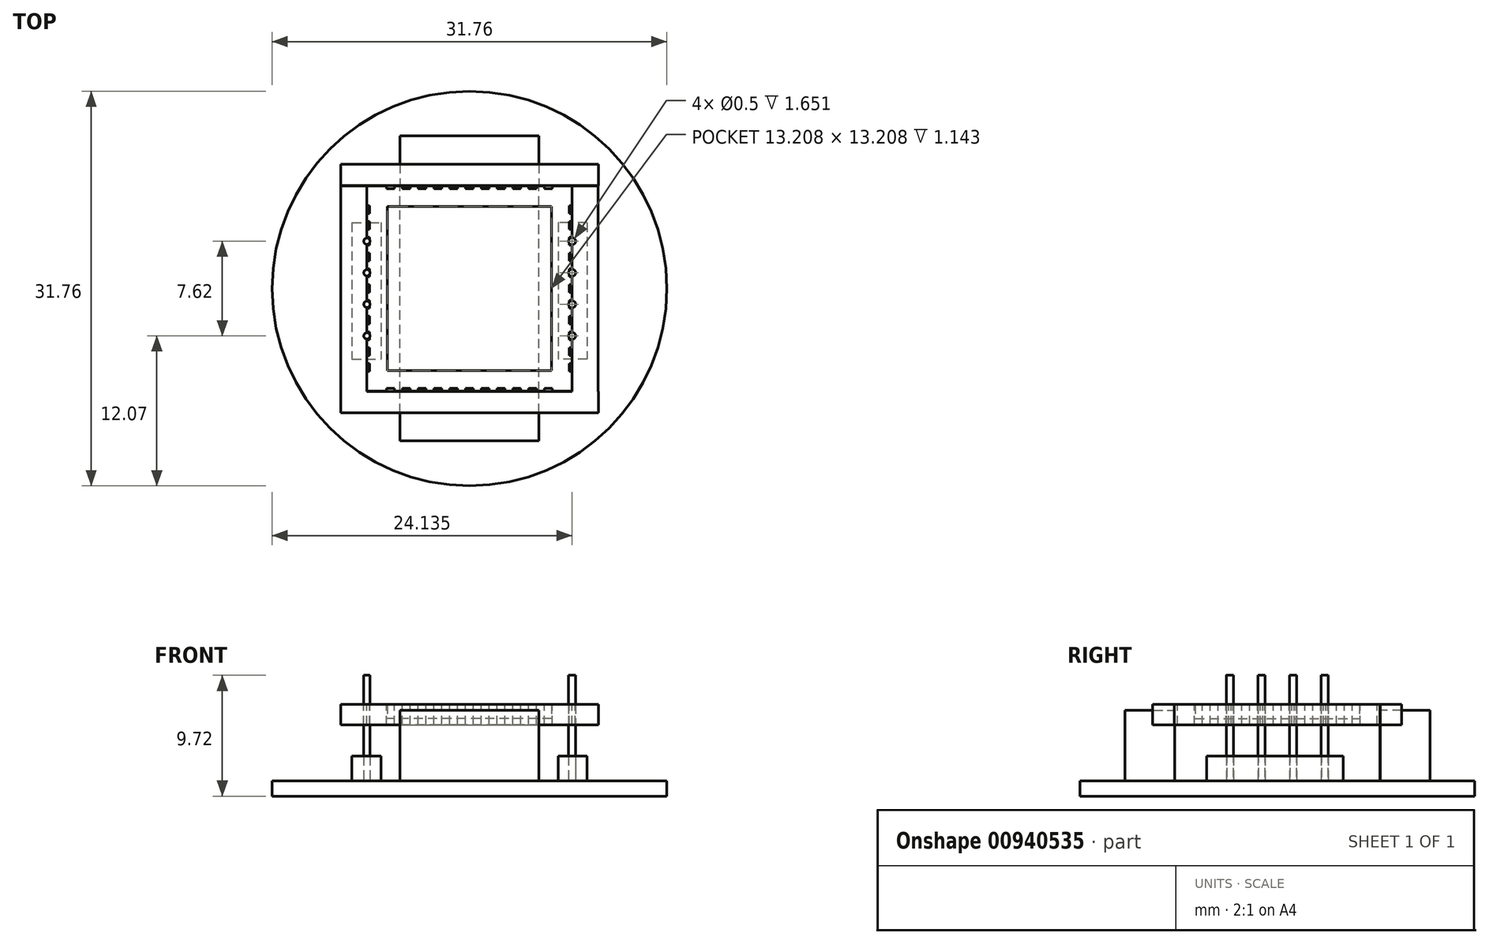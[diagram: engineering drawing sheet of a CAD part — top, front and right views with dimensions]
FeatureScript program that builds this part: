
annotation { "Feature Type Name" : "Feature", "Feature Type Description" : "" }
export const myFeature = defineFeature(function(context is Context, id is Id, definition is map)
    precondition{}
    {
        {
            var Q0;
            Q0=qCreatedBy(makeId("Top.planeOp"),FACE);
            var sketch = newSketch(context, id + "F0", { "sketchPlane" : qUnion([Q0])});
            skLineSegment(sketch, "E0.bottom", {"start": v(8.26, -8.26) * mm, "end": v(-8.26, -8.26) * mm});
            skLineSegment(sketch, "E0.top", {"start": v(8.26, 8.26) * mm, "end": v(-8.26, 8.26) * mm});
            skLineSegment(sketch, "E0.left", {"start": v(8.26, -8.26) * mm, "end": v(8.26, 8.26) * mm});
            skLineSegment(sketch, "E0.right", {"start": v(-8.26, -8.26) * mm, "end": v(-8.26, 8.26) * mm});
            skPoint(sketch, "E0.middle", {"position": v(0, 0) * mm});
            skLineSegment(sketch, "E1.bottom", {"start": v(6.6, -6.6) * mm, "end": v(-6.6, -6.6) * mm});
            skLineSegment(sketch, "E1.top", {"start": v(6.6, 6.6) * mm, "end": v(-6.6, 6.6) * mm});
            skLineSegment(sketch, "E1.left", {"start": v(6.6, -6.6) * mm, "end": v(6.6, 6.6) * mm});
            skLineSegment(sketch, "E1.right", {"start": v(-6.6, -6.6) * mm, "end": v(-6.6, 6.6) * mm});
            skSolve(sketch);
        }
        {
            var Q0;
            Q0=makeQuery(id+"F0.imprint","IMPRINT",FACE,{"disambiguationData":[TD([[makeQuery(id+"F0.imprint","IMPRINT",EDGE,{"derivedFrom":sQuery(id+"F0.wireOp",EDGE,"E1.bottom")}),-1.0]])]});
            extrude(context, id + "F1", {"entities" : qUnion([Q0]), "depth" : 0.5 * mm, "offsetDistance" : 25 * mm});
        }
        {
            var Q0;
            Q0=makeQuery(id+"F0.imprint","IMPRINT",FACE,{"disambiguationData":[TD([[makeQuery(id+"F0.imprint","IMPRINT",EDGE,{"derivedFrom":sQuery(id+"F0.wireOp",EDGE,"E0.bottom")}),-1.0]])]});
            extrude(context, id + "F2", {"entities" : qUnion([Q0]), "operationType" : NewBodyOperationType.ADD, "depth" : 1.65 * mm, "offsetDistance" : 25 * mm});
        }
        {
            var Q0;
            Q0=makeQuery(id+"F2.opExtrude","SWEPT_FACE",FACE,{"disambiguationData":[OSD([sQuery(id+"F0.wireOp",EDGE,"E0.bottom")])]});
            var sketch = newSketch(context, id + "F3", { "sketchPlane" : qUnion([Q0])});
            skLineSegment(sketch, "E2.bottom", {"start": v(-6.03, 0) * mm, "end": v(-6.67, 0) * mm});
            skLineSegment(sketch, "E2.top", {"start": v(-6.03, 1.65) * mm, "end": v(-6.67, 1.65) * mm});
            skLineSegment(sketch, "E2.left", {"start": v(-6.03, 0) * mm, "end": v(-6.03, 1.65) * mm});
            skLineSegment(sketch, "E2.right", {"start": v(-6.67, 0) * mm, "end": v(-6.67, 1.65) * mm});
            skPoint(sketch, "E2.middle", {"position": v(-6.35, 0.83) * mm});
            skLineSegment(sketch, "E3.bottom", {"start": v(-4.76, 0) * mm, "end": v(-5.4, 0) * mm});
            skLineSegment(sketch, "E3.top", {"start": v(-4.76, 1.65) * mm, "end": v(-5.4, 1.65) * mm});
            skLineSegment(sketch, "E3.left", {"start": v(-4.76, 0) * mm, "end": v(-4.76, 1.65) * mm});
            skLineSegment(sketch, "E3.right", {"start": v(-5.4, 0) * mm, "end": v(-5.4, 1.65) * mm});
            skPoint(sketch, "E3.middle", {"position": v(-5.08, 0.83) * mm});
            skLineSegment(sketch, "E4.MirrorCS", {"start": v(-4.13, 0) * mm, "end": v(-3.5, 0) * mm});
            skLineSegment(sketch, "E5.MirrorCS", {"start": v(-4.13, 1.65) * mm, "end": v(-3.5, 1.65) * mm});
            skPoint(sketch, "E6.MirrorP", {"position": v(-2.8, 0.8) * mm});
            skLineSegment(sketch, "E7.MirrorCS", {"start": v(-4.13, 0) * mm, "end": v(-4.13, 1.65) * mm});
            skLineSegment(sketch, "E8.MirrorCS", {"start": v(-2.86, 0) * mm, "end": v(-2.22, 0) * mm});
            skLineSegment(sketch, "E9.MirrorCS", {"start": v(-2.22, 0) * mm, "end": v(-2.22, 1.65) * mm});
            skLineSegment(sketch, "E10.MirrorCS", {"start": v(-2.86, 0) * mm, "end": v(-2.86, 1.65) * mm});
            skPoint(sketch, "E11.MirrorP", {"position": v(-4.1, 0.84) * mm});
            skLineSegment(sketch, "E12.MirrorCS", {"start": v(-3.5, 0) * mm, "end": v(-3.5, 1.65) * mm});
            skLineSegment(sketch, "E13.MirrorCS", {"start": v(-2.86, 1.65) * mm, "end": v(-2.22, 1.65) * mm});
            skLineSegment(sketch, "E14.MirrorCS", {"start": v(0.32, 0) * mm, "end": v(-0.32, 0) * mm});
            skPoint(sketch, "E15.MirrorP", {"position": v(-0.3, 0.84) * mm});
            skLineSegment(sketch, "E16.MirrorCS", {"start": v(-1.59, 0) * mm, "end": v(-1.59, 1.65) * mm});
            skLineSegment(sketch, "E17.MirrorCS", {"start": v(0.95, 0) * mm, "end": v(0.95, 1.65) * mm});
            skLineSegment(sketch, "E18.MirrorCS", {"start": v(-0.32, 0) * mm, "end": v(-0.32, 1.65) * mm});
            skLineSegment(sketch, "E19.MirrorCS", {"start": v(0.32, 0) * mm, "end": v(0.32, 1.65) * mm});
            skPoint(sketch, "E20.MirrorP", {"position": v(-1.56, 0.82) * mm});
            skLineSegment(sketch, "E21.MirrorCS", {"start": v(2.22, 1.65) * mm, "end": v(2.86, 1.65) * mm});
            skLineSegment(sketch, "E22.MirrorCS", {"start": v(2.86, 0) * mm, "end": v(2.86, 1.65) * mm});
            skLineSegment(sketch, "E23.MirrorCS", {"start": v(-0.95, 1.65) * mm, "end": v(-1.59, 1.65) * mm});
            skPoint(sketch, "E24.MirrorP", {"position": v(2.22, 0.83) * mm});
            skLineSegment(sketch, "E25.MirrorCS", {"start": v(-0.95, 0) * mm, "end": v(-1.59, 0) * mm});
            skLineSegment(sketch, "E26.MirrorCS", {"start": v(-0.95, 0) * mm, "end": v(-0.95, 1.65) * mm});
            skLineSegment(sketch, "E27.MirrorCS", {"start": v(0.95, 0) * mm, "end": v(1.59, 0) * mm});
            skLineSegment(sketch, "E28.MirrorCS", {"start": v(0.32, 1.65) * mm, "end": v(-0.32, 1.65) * mm});
            skLineSegment(sketch, "E29.MirrorCS", {"start": v(1.59, 0) * mm, "end": v(1.59, 1.65) * mm});
            skLineSegment(sketch, "E30.MirrorCS", {"start": v(0.95, 1.65) * mm, "end": v(1.59, 1.65) * mm});
            skLineSegment(sketch, "E31.MirrorCS", {"start": v(2.22, 0) * mm, "end": v(2.22, 1.65) * mm});
            skLineSegment(sketch, "E32.MirrorCS", {"start": v(2.22, 0) * mm, "end": v(2.86, 0) * mm});
            skPoint(sketch, "E33.MirrorP", {"position": v(0.95, 0.83) * mm});
            skLineSegment(sketch, "E34.MirrorCS", {"start": v(3.5, 0) * mm, "end": v(3.5, 1.65) * mm});
            skPoint(sketch, "E35.MirrorP", {"position": v(5.96, 0.82) * mm});
            skLineSegment(sketch, "E36.MirrorCS", {"start": v(6.03, 0) * mm, "end": v(6.67, 0) * mm});
            skLineSegment(sketch, "E37.MirrorCS", {"start": v(6.03, 0) * mm, "end": v(6.03, 1.65) * mm});
            skLineSegment(sketch, "E38.MirrorCS", {"start": v(5.4, 1.65) * mm, "end": v(4.76, 1.65) * mm});
            skPoint(sketch, "E39.MirrorP", {"position": v(4.76, 0.83) * mm});
            skLineSegment(sketch, "E40.MirrorCS", {"start": v(6.67, 0) * mm, "end": v(6.67, 1.65) * mm});
            skLineSegment(sketch, "E41.MirrorCS", {"start": v(5.4, 0) * mm, "end": v(5.4, 1.65) * mm});
            skLineSegment(sketch, "E42.MirrorCS", {"start": v(4.13, 0) * mm, "end": v(4.13, 1.65) * mm});
            skLineSegment(sketch, "E43.MirrorCS", {"start": v(4.76, 0) * mm, "end": v(4.76, 1.65) * mm});
            skLineSegment(sketch, "E44.MirrorCS", {"start": v(4.13, 0) * mm, "end": v(3.5, 0) * mm});
            skLineSegment(sketch, "E45.MirrorCS", {"start": v(5.4, 0) * mm, "end": v(4.76, 0) * mm});
            skLineSegment(sketch, "E46.MirrorCS", {"start": v(6.03, 1.65) * mm, "end": v(6.67, 1.65) * mm});
            skPoint(sketch, "E47.MirrorP", {"position": v(3.5, 0.83) * mm});
            skLineSegment(sketch, "E48.MirrorCS", {"start": v(4.13, 1.65) * mm, "end": v(3.5, 1.65) * mm});
            skLineSegment(sketch, "E49", {"start": v(-8.26, 0.83) * mm, "end": v(8.26, 0.83) * mm});
            skSolve(sketch);
        }
        {
            var Q0;
            {var subQ0=sQuery(id+"F3.wireOp",EDGE,"E2.top");Q0=makeQuery(id+"F3.imprint","IMPRINT",FACE,{"disambiguationData":[TD([[makeQuery(id+"F3.imprint","IMPRINT",EDGE,{"derivedFrom":subQ0}),1.0]])]});}
            var Q1;
            {var subQ0=sQuery(id+"F3.wireOp",EDGE,"E2.bottom");Q1=makeQuery(id+"F3.imprint","IMPRINT",FACE,{"disambiguationData":[TD([[makeQuery(id+"F3.imprint","IMPRINT",EDGE,{"derivedFrom":subQ0}),-1.0]])]});}
            var Q2;
            {var subQ0=sQuery(id+"F3.wireOp",EDGE,"E3.top");Q2=makeQuery(id+"F3.imprint","IMPRINT",FACE,{"disambiguationData":[TD([[makeQuery(id+"F3.imprint","IMPRINT",EDGE,{"derivedFrom":subQ0}),1.0]])]});}
            var Q3;
            {var subQ0=sQuery(id+"F3.wireOp",EDGE,"E3.bottom");Q3=makeQuery(id+"F3.imprint","IMPRINT",FACE,{"disambiguationData":[TD([[makeQuery(id+"F3.imprint","IMPRINT",EDGE,{"derivedFrom":subQ0}),-1.0]])]});}
            var Q4;
            {var subQ0=sQuery(id+"F3.wireOp",EDGE,"E5.MirrorCS");Q4=makeQuery(id+"F3.imprint","IMPRINT",FACE,{"disambiguationData":[TD([[makeQuery(id+"F3.imprint","IMPRINT",EDGE,{"derivedFrom":subQ0}),1.0]])]});}
            var Q5;
            {var subQ0=sQuery(id+"F3.wireOp",EDGE,"E4.MirrorCS");Q5=makeQuery(id+"F3.imprint","IMPRINT",FACE,{"disambiguationData":[TD([[makeQuery(id+"F3.imprint","IMPRINT",EDGE,{"derivedFrom":subQ0}),-1.0]])]});}
            var Q6;
            {var subQ0=sQuery(id+"F3.wireOp",EDGE,"E13.MirrorCS");Q6=makeQuery(id+"F3.imprint","IMPRINT",FACE,{"disambiguationData":[TD([[makeQuery(id+"F3.imprint","IMPRINT",EDGE,{"derivedFrom":subQ0}),1.0]])]});}
            var Q7;
            {var subQ0=sQuery(id+"F3.wireOp",EDGE,"E8.MirrorCS");Q7=makeQuery(id+"F3.imprint","IMPRINT",FACE,{"disambiguationData":[TD([[makeQuery(id+"F3.imprint","IMPRINT",EDGE,{"derivedFrom":subQ0}),-1.0]])]});}
            var Q8;
            {var subQ0=sQuery(id+"F3.wireOp",EDGE,"E23.MirrorCS");Q8=makeQuery(id+"F3.imprint","IMPRINT",FACE,{"disambiguationData":[TD([[makeQuery(id+"F3.imprint","IMPRINT",EDGE,{"derivedFrom":subQ0}),1.0]])]});}
            var Q9;
            {var subQ0=sQuery(id+"F3.wireOp",EDGE,"E25.MirrorCS");Q9=makeQuery(id+"F3.imprint","IMPRINT",FACE,{"disambiguationData":[TD([[makeQuery(id+"F3.imprint","IMPRINT",EDGE,{"derivedFrom":subQ0}),-1.0]])]});}
            var Q10;
            {var subQ0=sQuery(id+"F3.wireOp",EDGE,"E28.MirrorCS");Q10=makeQuery(id+"F3.imprint","IMPRINT",FACE,{"disambiguationData":[TD([[makeQuery(id+"F3.imprint","IMPRINT",EDGE,{"derivedFrom":subQ0}),1.0]])]});}
            var Q11;
            {var subQ0=sQuery(id+"F3.wireOp",EDGE,"E14.MirrorCS");Q11=makeQuery(id+"F3.imprint","IMPRINT",FACE,{"disambiguationData":[TD([[makeQuery(id+"F3.imprint","IMPRINT",EDGE,{"derivedFrom":subQ0}),-1.0]])]});}
            var Q12;
            {var subQ0=sQuery(id+"F3.wireOp",EDGE,"E30.MirrorCS");Q12=makeQuery(id+"F3.imprint","IMPRINT",FACE,{"disambiguationData":[TD([[makeQuery(id+"F3.imprint","IMPRINT",EDGE,{"derivedFrom":subQ0}),1.0]])]});}
            var Q13;
            {var subQ0=sQuery(id+"F3.wireOp",EDGE,"E27.MirrorCS");Q13=makeQuery(id+"F3.imprint","IMPRINT",FACE,{"disambiguationData":[TD([[makeQuery(id+"F3.imprint","IMPRINT",EDGE,{"derivedFrom":subQ0}),-1.0]])]});}
            var Q14;
            {var subQ0=sQuery(id+"F3.wireOp",EDGE,"E21.MirrorCS");Q14=makeQuery(id+"F3.imprint","IMPRINT",FACE,{"disambiguationData":[TD([[makeQuery(id+"F3.imprint","IMPRINT",EDGE,{"derivedFrom":subQ0}),1.0]])]});}
            var Q15;
            {var subQ0=sQuery(id+"F3.wireOp",EDGE,"E32.MirrorCS");Q15=makeQuery(id+"F3.imprint","IMPRINT",FACE,{"disambiguationData":[TD([[makeQuery(id+"F3.imprint","IMPRINT",EDGE,{"derivedFrom":subQ0}),-1.0]])]});}
            var Q16;
            {var subQ0=sQuery(id+"F3.wireOp",EDGE,"E48.MirrorCS");Q16=makeQuery(id+"F3.imprint","IMPRINT",FACE,{"disambiguationData":[TD([[makeQuery(id+"F3.imprint","IMPRINT",EDGE,{"derivedFrom":subQ0}),1.0]])]});}
            var Q17;
            {var subQ0=sQuery(id+"F3.wireOp",EDGE,"E44.MirrorCS");Q17=makeQuery(id+"F3.imprint","IMPRINT",FACE,{"disambiguationData":[TD([[makeQuery(id+"F3.imprint","IMPRINT",EDGE,{"derivedFrom":subQ0}),-1.0]])]});}
            var Q18;
            {var subQ0=sQuery(id+"F3.wireOp",EDGE,"E38.MirrorCS");Q18=makeQuery(id+"F3.imprint","IMPRINT",FACE,{"disambiguationData":[TD([[makeQuery(id+"F3.imprint","IMPRINT",EDGE,{"derivedFrom":subQ0}),1.0]])]});}
            var Q19;
            {var subQ0=sQuery(id+"F3.wireOp",EDGE,"E45.MirrorCS");Q19=makeQuery(id+"F3.imprint","IMPRINT",FACE,{"disambiguationData":[TD([[makeQuery(id+"F3.imprint","IMPRINT",EDGE,{"derivedFrom":subQ0}),-1.0]])]});}
            var Q20;
            {var subQ0=sQuery(id+"F3.wireOp",EDGE,"E46.MirrorCS");Q20=makeQuery(id+"F3.imprint","IMPRINT",FACE,{"disambiguationData":[TD([[makeQuery(id+"F3.imprint","IMPRINT",EDGE,{"derivedFrom":subQ0}),1.0]])]});}
            var Q21;
            {var subQ0=sQuery(id+"F3.wireOp",EDGE,"E36.MirrorCS");Q21=makeQuery(id+"F3.imprint","IMPRINT",FACE,{"disambiguationData":[TD([[makeQuery(id+"F3.imprint","IMPRINT",EDGE,{"derivedFrom":subQ0}),-1.0]])]});}
            extrude(context, id + "F4", {"entities" : qUnion([Q0, Q1, Q2, Q3, Q4, Q5, Q6, Q7, Q8, Q9, Q10, Q11, Q12, Q13, Q14, Q15, Q16, Q17, Q18, Q19, Q20, Q21]), "operationType" : NewBodyOperationType.REMOVE, "oppositeDirection" : true, "depth" : 0.23 * mm, "offsetDistance" : 25 * mm});
        }
        {
            var Q0;
            Q0=makeQuery(id+"F2.opExtrude","SWEPT_FACE",FACE,{"disambiguationData":[OSD([sQuery(id+"F0.wireOp",EDGE,"E0.left")])]});
            var sketch = newSketch(context, id + "F5", { "sketchPlane" : qUnion([Q0])});
            skLineSegment(sketch, "E50.bottom", {"start": v(-6.03, 0) * mm, "end": v(-6.67, 0) * mm});
            skLineSegment(sketch, "E50.top", {"start": v(-6.03, 1.65) * mm, "end": v(-6.67, 1.65) * mm});
            skLineSegment(sketch, "E50.left", {"start": v(-6.03, 0) * mm, "end": v(-6.03, 1.65) * mm});
            skLineSegment(sketch, "E50.right", {"start": v(-6.67, 0) * mm, "end": v(-6.67, 1.65) * mm});
            skPoint(sketch, "E50.middle", {"position": v(-6.35, 0.83) * mm});
            skLineSegment(sketch, "E51.bottom", {"start": v(-4.76, 0) * mm, "end": v(-5.4, 0) * mm});
            skLineSegment(sketch, "E51.top", {"start": v(-4.76, 1.65) * mm, "end": v(-5.4, 1.65) * mm});
            skLineSegment(sketch, "E51.left", {"start": v(-4.76, 0) * mm, "end": v(-4.76, 1.65) * mm});
            skLineSegment(sketch, "E51.right", {"start": v(-5.4, 0) * mm, "end": v(-5.4, 1.65) * mm});
            skPoint(sketch, "E51.middle", {"position": v(-5.08, 0.83) * mm});
            skLineSegment(sketch, "E52.MirrorCS", {"start": v(-4.13, 0) * mm, "end": v(-3.5, 0) * mm});
            skLineSegment(sketch, "E53.MirrorCS", {"start": v(-4.13, 1.65) * mm, "end": v(-3.5, 1.65) * mm});
            skPoint(sketch, "E54.MirrorP", {"position": v(-2.58, 0.8) * mm});
            skLineSegment(sketch, "E55.MirrorCS", {"start": v(-4.13, 0) * mm, "end": v(-4.13, 1.65) * mm});
            skLineSegment(sketch, "E56.MirrorCS", {"start": v(-2.86, 0) * mm, "end": v(-2.22, 0) * mm});
            skLineSegment(sketch, "E57.MirrorCS", {"start": v(-2.22, 0) * mm, "end": v(-2.22, 1.65) * mm});
            skLineSegment(sketch, "E58.MirrorCS", {"start": v(-2.86, 0) * mm, "end": v(-2.86, 1.65) * mm});
            skPoint(sketch, "E59.MirrorP", {"position": v(-3.88, 0.84) * mm});
            skLineSegment(sketch, "E60.MirrorCS", {"start": v(-3.5, 0) * mm, "end": v(-3.5, 1.65) * mm});
            skLineSegment(sketch, "E61.MirrorCS", {"start": v(-2.86, 1.65) * mm, "end": v(-2.22, 1.65) * mm});
            skLineSegment(sketch, "E62.MirrorCS", {"start": v(0.32, 0) * mm, "end": v(-0.32, 0) * mm});
            skPoint(sketch, "E63.MirrorP", {"position": v(-0.09, 0.84) * mm});
            skLineSegment(sketch, "E64.MirrorCS", {"start": v(-1.59, 0) * mm, "end": v(-1.59, 1.65) * mm});
            skLineSegment(sketch, "E65.MirrorCS", {"start": v(0.95, 0) * mm, "end": v(0.95, 1.65) * mm});
            skLineSegment(sketch, "E66.MirrorCS", {"start": v(-0.32, 0) * mm, "end": v(-0.32, 1.65) * mm});
            skLineSegment(sketch, "E67.MirrorCS", {"start": v(0.32, 0) * mm, "end": v(0.32, 1.65) * mm});
            skPoint(sketch, "E68.MirrorP", {"position": v(-1.34, 0.82) * mm});
            skLineSegment(sketch, "E69.MirrorCS", {"start": v(2.22, 1.65) * mm, "end": v(2.86, 1.65) * mm});
            skLineSegment(sketch, "E70.MirrorCS", {"start": v(2.86, 0) * mm, "end": v(2.86, 1.65) * mm});
            skLineSegment(sketch, "E71.MirrorCS", {"start": v(-0.95, 1.65) * mm, "end": v(-1.59, 1.65) * mm});
            skPoint(sketch, "E72.MirrorP", {"position": v(2.44, 0.83) * mm});
            skLineSegment(sketch, "E73.MirrorCS", {"start": v(-0.95, 0) * mm, "end": v(-1.59, 0) * mm});
            skLineSegment(sketch, "E74.MirrorCS", {"start": v(-0.95, 0) * mm, "end": v(-0.95, 1.65) * mm});
            skLineSegment(sketch, "E75.MirrorCS", {"start": v(0.95, 0) * mm, "end": v(1.59, 0) * mm});
            skLineSegment(sketch, "E76.MirrorCS", {"start": v(0.32, 1.65) * mm, "end": v(-0.32, 1.65) * mm});
            skLineSegment(sketch, "E77.MirrorCS", {"start": v(1.59, 0) * mm, "end": v(1.59, 1.65) * mm});
            skLineSegment(sketch, "E78.MirrorCS", {"start": v(0.95, 1.65) * mm, "end": v(1.59, 1.65) * mm});
            skLineSegment(sketch, "E79.MirrorCS", {"start": v(2.22, 0) * mm, "end": v(2.22, 1.65) * mm});
            skLineSegment(sketch, "E80.MirrorCS", {"start": v(2.22, 0) * mm, "end": v(2.86, 0) * mm});
            skPoint(sketch, "E81.MirrorP", {"position": v(1.17, 0.83) * mm});
            skLineSegment(sketch, "E82.MirrorCS", {"start": v(3.5, 0) * mm, "end": v(3.5, 1.65) * mm});
            skPoint(sketch, "E83.MirrorP", {"position": v(6.18, 0.82) * mm});
            skLineSegment(sketch, "E84.MirrorCS", {"start": v(6.03, 0) * mm, "end": v(6.67, 0) * mm});
            skLineSegment(sketch, "E85.MirrorCS", {"start": v(6.03, 0) * mm, "end": v(6.03, 1.65) * mm});
            skLineSegment(sketch, "E86.MirrorCS", {"start": v(5.4, 1.65) * mm, "end": v(4.76, 1.65) * mm});
            skPoint(sketch, "E87.MirrorP", {"position": v(4.98, 0.83) * mm});
            skLineSegment(sketch, "E88.MirrorCS", {"start": v(6.67, 0) * mm, "end": v(6.67, 1.65) * mm});
            skLineSegment(sketch, "E89.MirrorCS", {"start": v(5.4, 0) * mm, "end": v(5.4, 1.65) * mm});
            skLineSegment(sketch, "E90.MirrorCS", {"start": v(4.13, 0) * mm, "end": v(4.13, 1.65) * mm});
            skLineSegment(sketch, "E91.MirrorCS", {"start": v(4.76, 0) * mm, "end": v(4.76, 1.65) * mm});
            skLineSegment(sketch, "E92.MirrorCS", {"start": v(4.13, 0) * mm, "end": v(3.5, 0) * mm});
            skLineSegment(sketch, "E93.MirrorCS", {"start": v(5.4, 0) * mm, "end": v(4.76, 0) * mm});
            skLineSegment(sketch, "E94.MirrorCS", {"start": v(6.03, 1.65) * mm, "end": v(6.67, 1.65) * mm});
            skPoint(sketch, "E95.MirrorP", {"position": v(3.71, 0.83) * mm});
            skLineSegment(sketch, "E96.MirrorCS", {"start": v(4.13, 1.65) * mm, "end": v(3.5, 1.65) * mm});
            skLineSegment(sketch, "E97", {"start": v(-8.26, 0.83) * mm, "end": v(8.26, 0.83) * mm});
            skSolve(sketch);
        }
        {
            var Q0;
            {var subQ0=sQuery(id+"F5.wireOp",EDGE,"E51.bottom");Q0=makeQuery(id+"F5.imprint","IMPRINT",FACE,{"disambiguationData":[TD([[makeQuery(id+"F5.imprint","IMPRINT",EDGE,{"derivedFrom":subQ0}),-1.0]])]});}
            var Q1;
            {var subQ0=sQuery(id+"F5.wireOp",EDGE,"E52.MirrorCS");Q1=makeQuery(id+"F5.imprint","IMPRINT",FACE,{"disambiguationData":[TD([[makeQuery(id+"F5.imprint","IMPRINT",EDGE,{"derivedFrom":subQ0}),1.0]])]});}
            var Q2;
            {var subQ0=sQuery(id+"F5.wireOp",EDGE,"E56.MirrorCS");Q2=makeQuery(id+"F5.imprint","IMPRINT",FACE,{"disambiguationData":[TD([[makeQuery(id+"F5.imprint","IMPRINT",EDGE,{"derivedFrom":subQ0}),1.0]])]});}
            var Q3;
            {var subQ0=sQuery(id+"F5.wireOp",EDGE,"E62.MirrorCS");Q3=makeQuery(id+"F5.imprint","IMPRINT",FACE,{"disambiguationData":[TD([[makeQuery(id+"F5.imprint","IMPRINT",EDGE,{"derivedFrom":subQ0}),-1.0]])]});}
            var Q4;
            {var subQ0=sQuery(id+"F5.wireOp",EDGE,"E73.MirrorCS");Q4=makeQuery(id+"F5.imprint","IMPRINT",FACE,{"disambiguationData":[TD([[makeQuery(id+"F5.imprint","IMPRINT",EDGE,{"derivedFrom":subQ0}),-1.0]])]});}
            var Q5;
            {var subQ0=sQuery(id+"F5.wireOp",EDGE,"E75.MirrorCS");Q5=makeQuery(id+"F5.imprint","IMPRINT",FACE,{"disambiguationData":[TD([[makeQuery(id+"F5.imprint","IMPRINT",EDGE,{"derivedFrom":subQ0}),1.0]])]});}
            var Q6;
            {var subQ0=sQuery(id+"F5.wireOp",EDGE,"E80.MirrorCS");Q6=makeQuery(id+"F5.imprint","IMPRINT",FACE,{"disambiguationData":[TD([[makeQuery(id+"F5.imprint","IMPRINT",EDGE,{"derivedFrom":subQ0}),1.0]])]});}
            var Q7;
            {var subQ0=sQuery(id+"F5.wireOp",EDGE,"E92.MirrorCS");Q7=makeQuery(id+"F5.imprint","IMPRINT",FACE,{"disambiguationData":[TD([[makeQuery(id+"F5.imprint","IMPRINT",EDGE,{"derivedFrom":subQ0}),-1.0]])]});}
            var Q8;
            {var subQ0=sQuery(id+"F5.wireOp",EDGE,"E84.MirrorCS");Q8=makeQuery(id+"F5.imprint","IMPRINT",FACE,{"disambiguationData":[TD([[makeQuery(id+"F5.imprint","IMPRINT",EDGE,{"derivedFrom":subQ0}),1.0]])]});}
            var Q9;
            {var subQ0=sQuery(id+"F5.wireOp",EDGE,"E93.MirrorCS");Q9=makeQuery(id+"F5.imprint","IMPRINT",FACE,{"disambiguationData":[TD([[makeQuery(id+"F5.imprint","IMPRINT",EDGE,{"derivedFrom":subQ0}),-1.0]])]});}
            var Q10;
            {var subQ0=sQuery(id+"F5.wireOp",EDGE,"E50.top");Q10=makeQuery(id+"F5.imprint","IMPRINT",FACE,{"disambiguationData":[TD([[makeQuery(id+"F5.imprint","IMPRINT",EDGE,{"derivedFrom":subQ0}),1.0]])]});}
            var Q11;
            {var subQ0=sQuery(id+"F5.wireOp",EDGE,"E51.top");Q11=makeQuery(id+"F5.imprint","IMPRINT",FACE,{"disambiguationData":[TD([[makeQuery(id+"F5.imprint","IMPRINT",EDGE,{"derivedFrom":subQ0}),1.0]])]});}
            var Q12;
            {var subQ0=sQuery(id+"F5.wireOp",EDGE,"E53.MirrorCS");Q12=makeQuery(id+"F5.imprint","IMPRINT",FACE,{"disambiguationData":[TD([[makeQuery(id+"F5.imprint","IMPRINT",EDGE,{"derivedFrom":subQ0}),-1.0]])]});}
            var Q13;
            {var subQ0=sQuery(id+"F5.wireOp",EDGE,"E61.MirrorCS");Q13=makeQuery(id+"F5.imprint","IMPRINT",FACE,{"disambiguationData":[TD([[makeQuery(id+"F5.imprint","IMPRINT",EDGE,{"derivedFrom":subQ0}),-1.0]])]});}
            var Q14;
            {var subQ0=sQuery(id+"F5.wireOp",EDGE,"E71.MirrorCS");Q14=makeQuery(id+"F5.imprint","IMPRINT",FACE,{"disambiguationData":[TD([[makeQuery(id+"F5.imprint","IMPRINT",EDGE,{"derivedFrom":subQ0}),1.0]])]});}
            var Q15;
            {var subQ0=sQuery(id+"F5.wireOp",EDGE,"E78.MirrorCS");Q15=makeQuery(id+"F5.imprint","IMPRINT",FACE,{"disambiguationData":[TD([[makeQuery(id+"F5.imprint","IMPRINT",EDGE,{"derivedFrom":subQ0}),-1.0]])]});}
            var Q16;
            {var subQ0=sQuery(id+"F5.wireOp",EDGE,"E76.MirrorCS");Q16=makeQuery(id+"F5.imprint","IMPRINT",FACE,{"disambiguationData":[TD([[makeQuery(id+"F5.imprint","IMPRINT",EDGE,{"derivedFrom":subQ0}),1.0]])]});}
            var Q17;
            {var subQ0=sQuery(id+"F5.wireOp",EDGE,"E69.MirrorCS");Q17=makeQuery(id+"F5.imprint","IMPRINT",FACE,{"disambiguationData":[TD([[makeQuery(id+"F5.imprint","IMPRINT",EDGE,{"derivedFrom":subQ0}),-1.0]])]});}
            var Q18;
            {var subQ0=sQuery(id+"F5.wireOp",EDGE,"E96.MirrorCS");Q18=makeQuery(id+"F5.imprint","IMPRINT",FACE,{"disambiguationData":[TD([[makeQuery(id+"F5.imprint","IMPRINT",EDGE,{"derivedFrom":subQ0}),1.0]])]});}
            var Q19;
            {var subQ0=sQuery(id+"F5.wireOp",EDGE,"E94.MirrorCS");Q19=makeQuery(id+"F5.imprint","IMPRINT",FACE,{"disambiguationData":[TD([[makeQuery(id+"F5.imprint","IMPRINT",EDGE,{"derivedFrom":subQ0}),-1.0]])]});}
            var Q20;
            {var subQ0=sQuery(id+"F5.wireOp",EDGE,"E86.MirrorCS");Q20=makeQuery(id+"F5.imprint","IMPRINT",FACE,{"disambiguationData":[TD([[makeQuery(id+"F5.imprint","IMPRINT",EDGE,{"derivedFrom":subQ0}),1.0]])]});}
            var Q21;
            {var subQ0=sQuery(id+"F5.wireOp",EDGE,"E97");var subQ1=sQuery(id+"F5.wireOp",EDGE,"E51.left");var subQ2=makeQuery(id+"F5.imprint","INTERSECT",VERTEX,{"derivedFrom":[subQ1,subQ0]});Q21=makeQuery(id+"F5.imprint","IMPRINT",FACE,{"disambiguationData":[TD([[makeQuery(id+"F5.imprint","IMPRINT",EDGE,{"disambiguationData":[TD([[subQ2,-1.0]])],"derivedFrom":subQ1}),1.0]])]});}
            var Q22;
            {var subQ0=sQuery(id+"F5.wireOp",EDGE,"E97");var subQ1=sQuery(id+"F5.wireOp",EDGE,"E55.MirrorCS");var subQ2=makeQuery(id+"F5.imprint","INTERSECT",VERTEX,{"derivedFrom":[subQ1,subQ0]});Q22=makeQuery(id+"F5.imprint","IMPRINT",FACE,{"disambiguationData":[TD([[makeQuery(id+"F5.imprint","IMPRINT",EDGE,{"disambiguationData":[TD([[subQ2,-1.0]])],"derivedFrom":subQ1}),-1.0]])]});}
            var Q23;
            {var subQ0=sQuery(id+"F5.wireOp",EDGE,"E97");var subQ1=sQuery(id+"F5.wireOp",EDGE,"E57.MirrorCS");var subQ2=makeQuery(id+"F5.imprint","INTERSECT",VERTEX,{"derivedFrom":[subQ1,subQ0]});Q23=makeQuery(id+"F5.imprint","IMPRINT",FACE,{"disambiguationData":[TD([[makeQuery(id+"F5.imprint","IMPRINT",EDGE,{"disambiguationData":[TD([[subQ2,-1.0]])],"derivedFrom":subQ1}),1.0]])]});}
            var Q24;
            {var subQ0=sQuery(id+"F5.wireOp",EDGE,"E97");var subQ1=sQuery(id+"F5.wireOp",EDGE,"E64.MirrorCS");var subQ2=makeQuery(id+"F5.imprint","INTERSECT",VERTEX,{"derivedFrom":[subQ1,subQ0]});Q24=makeQuery(id+"F5.imprint","IMPRINT",FACE,{"disambiguationData":[TD([[makeQuery(id+"F5.imprint","IMPRINT",EDGE,{"disambiguationData":[TD([[subQ2,-1.0]])],"derivedFrom":subQ1}),-1.0]])]});}
            var Q25;
            {var subQ0=sQuery(id+"F5.wireOp",EDGE,"E97");var subQ1=sQuery(id+"F5.wireOp",EDGE,"E65.MirrorCS");var subQ2=makeQuery(id+"F5.imprint","INTERSECT",VERTEX,{"derivedFrom":[subQ1,subQ0]});Q25=makeQuery(id+"F5.imprint","IMPRINT",FACE,{"disambiguationData":[TD([[makeQuery(id+"F5.imprint","IMPRINT",EDGE,{"disambiguationData":[TD([[subQ2,-1.0]])],"derivedFrom":subQ1}),-1.0]])]});}
            var Q26;
            {var subQ0=sQuery(id+"F5.wireOp",EDGE,"E97");var subQ1=sQuery(id+"F5.wireOp",EDGE,"E66.MirrorCS");var subQ2=makeQuery(id+"F5.imprint","INTERSECT",VERTEX,{"derivedFrom":[subQ1,subQ0]});Q26=makeQuery(id+"F5.imprint","IMPRINT",FACE,{"disambiguationData":[TD([[makeQuery(id+"F5.imprint","IMPRINT",EDGE,{"disambiguationData":[TD([[subQ2,-1.0]])],"derivedFrom":subQ1}),-1.0]])]});}
            var Q27;
            {var subQ0=sQuery(id+"F5.wireOp",EDGE,"E97");var subQ1=sQuery(id+"F5.wireOp",EDGE,"E70.MirrorCS");var subQ2=makeQuery(id+"F5.imprint","INTERSECT",VERTEX,{"derivedFrom":[subQ1,subQ0]});Q27=makeQuery(id+"F5.imprint","IMPRINT",FACE,{"disambiguationData":[TD([[makeQuery(id+"F5.imprint","IMPRINT",EDGE,{"disambiguationData":[TD([[subQ2,-1.0]])],"derivedFrom":subQ1}),1.0]])]});}
            var Q28;
            {var subQ0=sQuery(id+"F5.wireOp",EDGE,"E97");var subQ1=sQuery(id+"F5.wireOp",EDGE,"E82.MirrorCS");var subQ2=makeQuery(id+"F5.imprint","INTERSECT",VERTEX,{"derivedFrom":[subQ1,subQ0]});Q28=makeQuery(id+"F5.imprint","IMPRINT",FACE,{"disambiguationData":[TD([[makeQuery(id+"F5.imprint","IMPRINT",EDGE,{"disambiguationData":[TD([[subQ2,-1.0]])],"derivedFrom":subQ1}),-1.0]])]});}
            var Q29;
            {var subQ0=sQuery(id+"F5.wireOp",EDGE,"E97");var subQ1=sQuery(id+"F5.wireOp",EDGE,"E85.MirrorCS");var subQ2=makeQuery(id+"F5.imprint","INTERSECT",VERTEX,{"derivedFrom":[subQ1,subQ0]});Q29=makeQuery(id+"F5.imprint","IMPRINT",FACE,{"disambiguationData":[TD([[makeQuery(id+"F5.imprint","IMPRINT",EDGE,{"disambiguationData":[TD([[subQ2,-1.0]])],"derivedFrom":subQ1}),-1.0]])]});}
            var Q30;
            {var subQ0=sQuery(id+"F5.wireOp",EDGE,"E97");var subQ1=sQuery(id+"F5.wireOp",EDGE,"E89.MirrorCS");var subQ2=makeQuery(id+"F5.imprint","INTERSECT",VERTEX,{"derivedFrom":[subQ1,subQ0]});Q30=makeQuery(id+"F5.imprint","IMPRINT",FACE,{"disambiguationData":[TD([[makeQuery(id+"F5.imprint","IMPRINT",EDGE,{"disambiguationData":[TD([[subQ2,-1.0]])],"derivedFrom":subQ1}),1.0]])]});}
            var Q31;
            {var subQ0=sQuery(id+"F5.wireOp",EDGE,"E97");var subQ1=sQuery(id+"F5.wireOp",EDGE,"E50.left");var subQ2=makeQuery(id+"F5.imprint","INTERSECT",VERTEX,{"derivedFrom":[subQ1,subQ0]});Q31=makeQuery(id+"F5.imprint","IMPRINT",FACE,{"disambiguationData":[TD([[makeQuery(id+"F5.imprint","IMPRINT",EDGE,{"disambiguationData":[TD([[subQ2,-1.0]])],"derivedFrom":subQ1}),1.0]])]});}
            var Q32;
            {var subQ0=sQuery(id+"F5.wireOp",EDGE,"E50.bottom");Q32=makeQuery(id+"F5.imprint","IMPRINT",FACE,{"disambiguationData":[TD([[makeQuery(id+"F5.imprint","IMPRINT",EDGE,{"derivedFrom":subQ0}),-1.0]])]});}
            extrude(context, id + "F6", {"entities" : qUnion([Q0, Q1, Q2, Q3, Q4, Q5, Q6, Q7, Q8, Q9, Q10, Q11, Q12, Q13, Q14, Q15, Q16, Q17, Q18, Q19, Q20, Q21, Q22, Q23, Q24, Q25, Q26, Q27, Q28, Q29, Q30, Q31, Q32]), "operationType" : NewBodyOperationType.REMOVE, "oppositeDirection" : true, "depth" : 0.23 * mm, "offsetDistance" : 25 * mm});
        }
        {
            var Q0;
            Q0=makeQuery(id+"F2.opExtrude","SWEPT_FACE",FACE,{"disambiguationData":[OSD([sQuery(id+"F0.wireOp",EDGE,"E0.top")])]});
            var sketch = newSketch(context, id + "F7", { "sketchPlane" : qUnion([Q0])});
            skLineSegment(sketch, "E98.bottom", {"start": v(-6.03, 0) * mm, "end": v(-6.67, 0) * mm});
            skLineSegment(sketch, "E98.top", {"start": v(-6.03, 1.65) * mm, "end": v(-6.67, 1.65) * mm});
            skLineSegment(sketch, "E98.left", {"start": v(-6.03, 0) * mm, "end": v(-6.03, 1.65) * mm});
            skLineSegment(sketch, "E98.right", {"start": v(-6.67, 0) * mm, "end": v(-6.67, 1.65) * mm});
            skPoint(sketch, "E98.middle", {"position": v(-6.35, 0.83) * mm});
            skLineSegment(sketch, "E99.bottom", {"start": v(-4.76, 0) * mm, "end": v(-5.4, 0) * mm});
            skLineSegment(sketch, "E99.top", {"start": v(-4.76, 1.65) * mm, "end": v(-5.4, 1.65) * mm});
            skLineSegment(sketch, "E99.left", {"start": v(-4.76, 0) * mm, "end": v(-4.76, 1.65) * mm});
            skLineSegment(sketch, "E99.right", {"start": v(-5.4, 0) * mm, "end": v(-5.4, 1.65) * mm});
            skPoint(sketch, "E99.middle", {"position": v(-5.08, 0.83) * mm});
            skLineSegment(sketch, "E100.MirrorCS", {"start": v(-4.13, 0) * mm, "end": v(-3.5, 0) * mm});
            skLineSegment(sketch, "E101.MirrorCS", {"start": v(-4.13, 1.65) * mm, "end": v(-3.5, 1.65) * mm});
            skPoint(sketch, "E102.MirrorP", {"position": v(-2.8, 0.8) * mm});
            skLineSegment(sketch, "E103.MirrorCS", {"start": v(-4.13, 0) * mm, "end": v(-4.13, 1.65) * mm});
            skLineSegment(sketch, "E104.MirrorCS", {"start": v(-2.86, 0) * mm, "end": v(-2.22, 0) * mm});
            skLineSegment(sketch, "E105.MirrorCS", {"start": v(-2.22, 0) * mm, "end": v(-2.22, 1.65) * mm});
            skLineSegment(sketch, "E106.MirrorCS", {"start": v(-2.86, 0) * mm, "end": v(-2.86, 1.65) * mm});
            skPoint(sketch, "E107.MirrorP", {"position": v(-4.1, 0.84) * mm});
            skLineSegment(sketch, "E108.MirrorCS", {"start": v(-3.5, 0) * mm, "end": v(-3.5, 1.65) * mm});
            skLineSegment(sketch, "E109.MirrorCS", {"start": v(-2.86, 1.65) * mm, "end": v(-2.22, 1.65) * mm});
            skLineSegment(sketch, "E110.MirrorCS", {"start": v(0.32, 0) * mm, "end": v(-0.32, 0) * mm});
            skPoint(sketch, "E111.MirrorP", {"position": v(-0.3, 0.84) * mm});
            skLineSegment(sketch, "E112.MirrorCS", {"start": v(-1.59, 0) * mm, "end": v(-1.59, 1.65) * mm});
            skLineSegment(sketch, "E113.MirrorCS", {"start": v(0.95, 0) * mm, "end": v(0.95, 1.65) * mm});
            skLineSegment(sketch, "E114.MirrorCS", {"start": v(-0.32, 0) * mm, "end": v(-0.32, 1.65) * mm});
            skLineSegment(sketch, "E115.MirrorCS", {"start": v(0.32, 0) * mm, "end": v(0.32, 1.65) * mm});
            skPoint(sketch, "E116.MirrorP", {"position": v(-1.56, 0.82) * mm});
            skLineSegment(sketch, "E117.MirrorCS", {"start": v(2.22, 1.65) * mm, "end": v(2.86, 1.65) * mm});
            skLineSegment(sketch, "E118.MirrorCS", {"start": v(2.86, 0) * mm, "end": v(2.86, 1.65) * mm});
            skLineSegment(sketch, "E119.MirrorCS", {"start": v(-0.95, 1.65) * mm, "end": v(-1.59, 1.65) * mm});
            skPoint(sketch, "E120.MirrorP", {"position": v(2.22, 0.83) * mm});
            skLineSegment(sketch, "E121.MirrorCS", {"start": v(-0.95, 0) * mm, "end": v(-1.59, 0) * mm});
            skLineSegment(sketch, "E122.MirrorCS", {"start": v(-0.95, 0) * mm, "end": v(-0.95, 1.65) * mm});
            skLineSegment(sketch, "E123.MirrorCS", {"start": v(0.95, 0) * mm, "end": v(1.59, 0) * mm});
            skLineSegment(sketch, "E124.MirrorCS", {"start": v(0.32, 1.65) * mm, "end": v(-0.32, 1.65) * mm});
            skLineSegment(sketch, "E125.MirrorCS", {"start": v(1.59, 0) * mm, "end": v(1.59, 1.65) * mm});
            skLineSegment(sketch, "E126.MirrorCS", {"start": v(0.95, 1.65) * mm, "end": v(1.59, 1.65) * mm});
            skLineSegment(sketch, "E127.MirrorCS", {"start": v(2.22, 0) * mm, "end": v(2.22, 1.65) * mm});
            skLineSegment(sketch, "E128.MirrorCS", {"start": v(2.22, 0) * mm, "end": v(2.86, 0) * mm});
            skPoint(sketch, "E129.MirrorP", {"position": v(0.95, 0.83) * mm});
            skLineSegment(sketch, "E130.MirrorCS", {"start": v(3.5, 0) * mm, "end": v(3.5, 1.65) * mm});
            skPoint(sketch, "E131.MirrorP", {"position": v(5.96, 0.82) * mm});
            skLineSegment(sketch, "E132.MirrorCS", {"start": v(6.03, 0) * mm, "end": v(6.67, 0) * mm});
            skLineSegment(sketch, "E133.MirrorCS", {"start": v(6.03, 0) * mm, "end": v(6.03, 1.65) * mm});
            skLineSegment(sketch, "E134.MirrorCS", {"start": v(5.4, 1.65) * mm, "end": v(4.76, 1.65) * mm});
            skPoint(sketch, "E135.MirrorP", {"position": v(4.76, 0.83) * mm});
            skLineSegment(sketch, "E136.MirrorCS", {"start": v(6.67, 0) * mm, "end": v(6.67, 1.65) * mm});
            skLineSegment(sketch, "E137.MirrorCS", {"start": v(5.4, 0) * mm, "end": v(5.4, 1.65) * mm});
            skLineSegment(sketch, "E138.MirrorCS", {"start": v(4.13, 0) * mm, "end": v(4.13, 1.65) * mm});
            skLineSegment(sketch, "E139.MirrorCS", {"start": v(4.76, 0) * mm, "end": v(4.76, 1.65) * mm});
            skLineSegment(sketch, "E140.MirrorCS", {"start": v(4.13, 0) * mm, "end": v(3.5, 0) * mm});
            skLineSegment(sketch, "E141.MirrorCS", {"start": v(5.4, 0) * mm, "end": v(4.76, 0) * mm});
            skLineSegment(sketch, "E142.MirrorCS", {"start": v(6.03, 1.65) * mm, "end": v(6.67, 1.65) * mm});
            skPoint(sketch, "E143.MirrorP", {"position": v(3.5, 0.83) * mm});
            skLineSegment(sketch, "E144.MirrorCS", {"start": v(4.13, 1.65) * mm, "end": v(3.5, 1.65) * mm});
            skLineSegment(sketch, "E145", {"start": v(-8.26, 0.83) * mm, "end": v(8.26, 0.83) * mm});
            skSolve(sketch);
        }
        {
            var Q0;
            Q0=qSketchRegion(id+"F7",true);
            extrude(context, id + "F8", {"entities" : qUnion([Q0]), "operationType" : NewBodyOperationType.REMOVE, "oppositeDirection" : true, "depth" : 0.23 * mm, "offsetDistance" : 25 * mm});
        }
        {
            var Q0;
            Q0=makeQuery(id+"F2.opExtrude","SWEPT_FACE",FACE,{"disambiguationData":[OSD([sQuery(id+"F0.wireOp",EDGE,"E0.right")])]});
            var sketch = newSketch(context, id + "F9", { "sketchPlane" : qUnion([Q0])});
            skLineSegment(sketch, "E146.bottom", {"start": v(-6.03, 0) * mm, "end": v(-6.67, 0) * mm});
            skLineSegment(sketch, "E146.top", {"start": v(-6.03, 1.65) * mm, "end": v(-6.67, 1.65) * mm});
            skLineSegment(sketch, "E146.left", {"start": v(-6.03, 0) * mm, "end": v(-6.03, 1.65) * mm});
            skLineSegment(sketch, "E146.right", {"start": v(-6.67, 0) * mm, "end": v(-6.67, 1.65) * mm});
            skPoint(sketch, "E146.middle", {"position": v(-6.35, 0.82) * mm});
            skLineSegment(sketch, "E147.bottom", {"start": v(-4.76, 0) * mm, "end": v(-5.4, 0) * mm});
            skLineSegment(sketch, "E147.top", {"start": v(-4.76, 1.65) * mm, "end": v(-5.4, 1.65) * mm});
            skLineSegment(sketch, "E147.left", {"start": v(-4.76, 0) * mm, "end": v(-4.76, 1.65) * mm});
            skLineSegment(sketch, "E147.right", {"start": v(-5.4, 0) * mm, "end": v(-5.4, 1.65) * mm});
            skPoint(sketch, "E147.middle", {"position": v(-5.08, 0.82) * mm});
            skLineSegment(sketch, "E148.MirrorCS", {"start": v(-4.13, 0) * mm, "end": v(-3.5, 0) * mm});
            skLineSegment(sketch, "E149.MirrorCS", {"start": v(-4.13, 1.65) * mm, "end": v(-3.5, 1.65) * mm});
            skPoint(sketch, "E150.MirrorP", {"position": v(-2.8, 0.8) * mm});
            skLineSegment(sketch, "E151.MirrorCS", {"start": v(-4.13, 0) * mm, "end": v(-4.13, 1.65) * mm});
            skLineSegment(sketch, "E152.MirrorCS", {"start": v(-2.86, 0) * mm, "end": v(-2.22, 0) * mm});
            skLineSegment(sketch, "E153.MirrorCS", {"start": v(-2.22, 0) * mm, "end": v(-2.22, 1.65) * mm});
            skLineSegment(sketch, "E154.MirrorCS", {"start": v(-2.86, 0) * mm, "end": v(-2.86, 1.65) * mm});
            skPoint(sketch, "E155.MirrorP", {"position": v(-4.1, 0.84) * mm});
            skLineSegment(sketch, "E156.MirrorCS", {"start": v(-3.5, 0) * mm, "end": v(-3.5, 1.65) * mm});
            skLineSegment(sketch, "E157.MirrorCS", {"start": v(-2.86, 1.65) * mm, "end": v(-2.22, 1.65) * mm});
            skLineSegment(sketch, "E158.MirrorCS", {"start": v(0.32, 0) * mm, "end": v(-0.32, 0) * mm});
            skPoint(sketch, "E159.MirrorP", {"position": v(-0.3, 0.84) * mm});
            skLineSegment(sketch, "E160.MirrorCS", {"start": v(-1.59, 0) * mm, "end": v(-1.59, 1.65) * mm});
            skLineSegment(sketch, "E161.MirrorCS", {"start": v(0.95, 0) * mm, "end": v(0.95, 1.65) * mm});
            skLineSegment(sketch, "E162.MirrorCS", {"start": v(-0.32, 0) * mm, "end": v(-0.32, 1.65) * mm});
            skLineSegment(sketch, "E163.MirrorCS", {"start": v(0.32, 0) * mm, "end": v(0.32, 1.65) * mm});
            skPoint(sketch, "E164.MirrorP", {"position": v(-1.56, 0.81) * mm});
            skLineSegment(sketch, "E165.MirrorCS", {"start": v(2.22, 1.65) * mm, "end": v(2.86, 1.65) * mm});
            skLineSegment(sketch, "E166.MirrorCS", {"start": v(2.86, 0) * mm, "end": v(2.86, 1.65) * mm});
            skLineSegment(sketch, "E167.MirrorCS", {"start": v(-0.95, 1.65) * mm, "end": v(-1.59, 1.65) * mm});
            skPoint(sketch, "E168.MirrorP", {"position": v(2.22, 0.82) * mm});
            skLineSegment(sketch, "E169.MirrorCS", {"start": v(-0.95, 0) * mm, "end": v(-1.59, 0) * mm});
            skLineSegment(sketch, "E170.MirrorCS", {"start": v(-0.95, 0) * mm, "end": v(-0.95, 1.65) * mm});
            skLineSegment(sketch, "E171.MirrorCS", {"start": v(0.95, 0) * mm, "end": v(1.59, 0) * mm});
            skLineSegment(sketch, "E172.MirrorCS", {"start": v(0.32, 1.65) * mm, "end": v(-0.32, 1.65) * mm});
            skLineSegment(sketch, "E173.MirrorCS", {"start": v(1.59, 0) * mm, "end": v(1.59, 1.65) * mm});
            skLineSegment(sketch, "E174.MirrorCS", {"start": v(0.95, 1.65) * mm, "end": v(1.59, 1.65) * mm});
            skLineSegment(sketch, "E175.MirrorCS", {"start": v(2.22, 0) * mm, "end": v(2.22, 1.65) * mm});
            skLineSegment(sketch, "E176.MirrorCS", {"start": v(2.22, 0) * mm, "end": v(2.86, 0) * mm});
            skPoint(sketch, "E177.MirrorP", {"position": v(0.95, 0.82) * mm});
            skLineSegment(sketch, "E178.MirrorCS", {"start": v(3.5, 0) * mm, "end": v(3.5, 1.65) * mm});
            skPoint(sketch, "E179.MirrorP", {"position": v(5.96, 0.81) * mm});
            skLineSegment(sketch, "E180.MirrorCS", {"start": v(6.03, 0) * mm, "end": v(6.67, 0) * mm});
            skLineSegment(sketch, "E181.MirrorCS", {"start": v(6.03, 0) * mm, "end": v(6.03, 1.65) * mm});
            skLineSegment(sketch, "E182.MirrorCS", {"start": v(5.4, 1.65) * mm, "end": v(4.76, 1.65) * mm});
            skPoint(sketch, "E183.MirrorP", {"position": v(4.76, 0.82) * mm});
            skLineSegment(sketch, "E184.MirrorCS", {"start": v(6.67, 0) * mm, "end": v(6.67, 1.65) * mm});
            skLineSegment(sketch, "E185.MirrorCS", {"start": v(5.4, 0) * mm, "end": v(5.4, 1.65) * mm});
            skLineSegment(sketch, "E186.MirrorCS", {"start": v(4.13, 0) * mm, "end": v(4.13, 1.65) * mm});
            skLineSegment(sketch, "E187.MirrorCS", {"start": v(4.76, 0) * mm, "end": v(4.76, 1.65) * mm});
            skLineSegment(sketch, "E188.MirrorCS", {"start": v(4.13, 0) * mm, "end": v(3.5, 0) * mm});
            skLineSegment(sketch, "E189.MirrorCS", {"start": v(5.4, 0) * mm, "end": v(4.76, 0) * mm});
            skLineSegment(sketch, "E190.MirrorCS", {"start": v(6.03, 1.65) * mm, "end": v(6.67, 1.65) * mm});
            skPoint(sketch, "E191.MirrorP", {"position": v(3.5, 0.82) * mm});
            skLineSegment(sketch, "E192.MirrorCS", {"start": v(4.13, 1.65) * mm, "end": v(3.5, 1.65) * mm});
            skLineSegment(sketch, "E193", {"start": v(-8.26, 0.82) * mm, "end": v(8.25, 0.82) * mm});
            skSolve(sketch);
        }
        {
            var Q0;
            Q0=qSketchRegion(id+"F9",true);
            extrude(context, id + "F10", {"entities" : qUnion([Q0]), "operationType" : NewBodyOperationType.REMOVE, "oppositeDirection" : true, "depth" : 0.23 * mm, "offsetDistance" : 25 * mm});
        }
        {
            var Q0;
            {var subQ0=sQuery(id+"F0.wireOp",EDGE,"E1.right");var subQ1=sQuery(id+"F0.wireOp",EDGE,"E1.left");var subQ2=sQuery(id+"F0.wireOp",EDGE,"E1.top");var subQ3=sQuery(id+"F0.wireOp",EDGE,"E1.bottom");Q0=makeQuery(id+"F2.boolean.opBoolean","MERGE",FACE,{"derivedFrom":[makeQuery(id+"F1.opExtrude","CAP_FACE",FACE,{"disambiguationData":[OSD([subQ3,subQ2,subQ1,subQ0])],"isStart":true}),makeQuery(id+"F2.opExtrude","CAP_FACE",FACE,{"disambiguationData":[OSD([sQuery(id+"F0.wireOp",EDGE,"E0.bottom"),sQuery(id+"F0.wireOp",EDGE,"E0.top"),sQuery(id+"F0.wireOp",EDGE,"E0.left"),sQuery(id+"F0.wireOp",EDGE,"E0.right"),subQ3,subQ2,subQ1,subQ0])],"isStart":true})]});}
            var sketch = newSketch(context, id + "F11", { "sketchPlane" : qUnion([Q0])});
            skCircle(sketch, "E194", {"center": v(0, 0) * mm, "radius": 15.88 * mm});
            skSolve(sketch);
        }
        {
            var Q0;
            Q0 = qSketchRegion(id + "F11", true);
            extrude(context, id + "F12", {"entities" : qUnion([Q0]), "depth" : 6.35 * mm, "offsetDistance" : 25 * mm});
        }
        {
            var Q0;
            Q0=makeQuery(id+"F12.opExtrude","CAP_FACE",FACE,{"disambiguationData":[OSD([sQuery(id+"F11.wireOp",EDGE,"E194")])],"isStart":true});
            var sketch = newSketch(context, id + "F13", { "sketchPlane" : qUnion([Q0])});
            skCircle(sketch, "E195", {"center": v(0, 0) * mm, "radius": 15.88 * mm});
            skSolve(sketch);
        }
        {
            var Q0;
            Q0=makeQuery(id+"F13.imprint","IMPRINT",FACE,{"disambiguationData":[TD([[makeQuery(id+"F13.imprint","IMPRINT",EDGE,{"derivedFrom":sQuery(id+"F13.wireOp",EDGE,"E195")}),-1.0]])]});
            extrude(context, id + "F14", {"entities" : qUnion([Q0]), "operationType" : NewBodyOperationType.REMOVE, "oppositeDirection" : true, "depth" : 5.13 * mm, "offsetDistance" : 25 * mm});
        }
        {
            var Q0;
            Q0=makeQuery(id+"F14.boolean.opBoolean","COPY",FACE,{"derivedFrom":makeQuery(id+"F14.opExtrude","CAP_FACE",FACE,{"disambiguationData":[OSD([sQuery(id+"F13.wireOp",EDGE,"E195")])],"isStart":false})});
            var sketch = newSketch(context, id + "F15", { "sketchPlane" : qUnion([Q0])});
            skLineSegment(sketch, "E196.bottom", {"start": v(5.59, -8.26) * mm, "end": v(-5.59, -8.26) * mm});
            skLineSegment(sketch, "E196.top", {"start": v(5.59, 8.26) * mm, "end": v(-5.59, 8.26) * mm});
            skLineSegment(sketch, "E196.left", {"start": v(5.59, -8.26) * mm, "end": v(5.59, 8.26) * mm});
            skLineSegment(sketch, "E196.right", {"start": v(-5.59, -8.26) * mm, "end": v(-5.59, 8.26) * mm});
            skPoint(sketch, "E196.middle", {"position": v(0, 0) * mm});
            skLineSegment(sketch, "E197", {"start": v(8.43, -0.62) * mm, "end": v(6.27, -0.62) * mm});
            skSolve(sketch);
        }
        {
            var Q0;
            Q0 = qSketchRegion(id + "F15", true);
            extrude(context, id + "F16", {"entities" : qUnion([Q0]), "depth" : 4.5 * mm, "offsetDistance" : 25 * mm});
        }
        {
            var Q0;
            Q0=makeQuery(id+"F16.opExtrude","SWEPT_BODY",BODY,{"disambiguationData":[OSD([sQuery(id+"F15.wireOp",EDGE,"E196.bottom"),sQuery(id+"F15.wireOp",EDGE,"E196.top"),sQuery(id+"F15.wireOp",EDGE,"E196.left"),sQuery(id+"F15.wireOp",EDGE,"E196.right")])]});
            transform(context, id + "F17", {"entities" : qUnion([Q0]), "transformType" : TransformType.TRANSLATION_3D, "dx" : 0 * mm, "dy" : 0 * mm, "dz" : 0.62 * mm, "makeCopy" : false});
        }
        {
            var Q0;
            Q0=makeQuery(id+"F12.opExtrude","SWEPT_BODY",BODY,{"disambiguationData":[OSD([sQuery(id+"F11.wireOp",EDGE,"E194")])]});
            transform(context, id + "F18", {"entities" : qUnion([Q0]), "transformType" : TransformType.TRANSLATION_3D, "dx" : 0 * mm, "dy" : 0 * mm, "dz" : 0.62 * mm, "makeCopy" : false});
        }
        {
            var Q0;
            Q0=makeQuery(id+"F14.boolean.opBoolean","COPY",FACE,{"derivedFrom":makeQuery(id+"F14.opExtrude","CAP_FACE",FACE,{"disambiguationData":[OSD([sQuery(id+"F13.wireOp",EDGE,"E195")])],"isStart":false})});
            var sketch = newSketch(context, id + "F19", { "sketchPlane" : qUnion([Q0])});
            skLineSegment(sketch, "E198", {"start": v(-8.25, 6.6) * mm, "end": v(-8.25, -6.02) * mm});
            skLineSegment(sketch, "E199", {"start": v(8.25, 6.73) * mm, "end": v(8.25, -5.45) * mm});
            skCircle(sketch, "E200", {"center": v(-8.25, 3.8) * mm, "radius": 0.25 * mm});
            skCircle(sketch, "E201", {"center": v(-8.25, 1.27) * mm, "radius": 0.25 * mm});
            skCircle(sketch, "E202", {"center": v(-8.25, -1.27) * mm, "radius": 0.25 * mm});
            skCircle(sketch, "E203", {"center": v(-8.25, -3.81) * mm, "radius": 0.25 * mm});
            skCircle(sketch, "E204.MirrorC", {"center": v(8.25, 1.27) * mm, "radius": 0.28 * mm});
            skCircle(sketch, "E205.MirrorC", {"center": v(8.25, 3.8) * mm, "radius": 0.28 * mm});
            skCircle(sketch, "E206.MirrorC", {"center": v(8.25, -1.27) * mm, "radius": 0.28 * mm});
            skCircle(sketch, "E207.MirrorC", {"center": v(8.25, -3.81) * mm, "radius": 0.28 * mm});
            skSolve(sketch);
        }
        {
            var Q0;
            Q0 = qSketchRegion(id + "F19", true);
            extrude(context, id + "F20", {"entities" : qUnion([Q0]), "depth" : 8.5 * mm, "offsetDistance" : 25 * mm});
        }
        {
            var Q0;
            Q0=makeQuery(id+"F14.boolean.opBoolean","COPY",FACE,{"derivedFrom":makeQuery(id+"F14.opExtrude","CAP_FACE",FACE,{"disambiguationData":[OSD([sQuery(id+"F13.wireOp",EDGE,"E195")])],"isStart":false})});
            var sketch = newSketch(context, id + "F21", { "sketchPlane" : qUnion([Q0])});
            skLineSegment(sketch, "E208.bottom", {"start": v(-9.46, 5.3) * mm, "end": v(-7.13, 5.3) * mm});
            skLineSegment(sketch, "E208.top", {"start": v(-9.46, -5.67) * mm, "end": v(-7.13, -5.67) * mm});
            skLineSegment(sketch, "E208.left", {"start": v(-9.46, 5.3) * mm, "end": v(-9.46, -5.67) * mm});
            skLineSegment(sketch, "E208.right", {"start": v(-7.13, 5.3) * mm, "end": v(-7.13, -5.67) * mm});
            skLineSegment(sketch, "E209.MirrorCS", {"start": v(9.46, 5.3) * mm, "end": v(7.13, 5.3) * mm});
            skLineSegment(sketch, "E210.MirrorCS", {"start": v(9.46, 5.3) * mm, "end": v(9.46, -5.67) * mm});
            skLineSegment(sketch, "E211.MirrorCS", {"start": v(7.13, 5.3) * mm, "end": v(7.13, -5.67) * mm});
            skLineSegment(sketch, "E212.MirrorCS", {"start": v(9.46, -5.67) * mm, "end": v(7.13, -5.67) * mm});
            skSolve(sketch);
        }
        {
            var Q0;
            Q0 = qSketchRegion(id + "F21", true);
            extrude(context, id + "F22", {"entities" : qUnion([Q0]), "depth" : 2 * mm, "offsetDistance" : 25 * mm});
        }
        {
            var Q0;
            Q0=makeQuery(id+"F14.boolean.opBoolean","COPY",FACE,{"derivedFrom":makeQuery(id+"F14.opExtrude","CAP_FACE",FACE,{"disambiguationData":[OSD([sQuery(id+"F13.wireOp",EDGE,"E195")])],"isStart":false})});
            var sketch = newSketch(context, id + "F23", { "sketchPlane" : qUnion([Q0])});
            skLineSegment(sketch, "E213.bottom", {"start": v(5.59, -12.26) * mm, "end": v(-5.59, -12.26) * mm});
            skLineSegment(sketch, "E213.top", {"start": v(5.59, -8.26) * mm, "end": v(-5.59, -8.26) * mm});
            skLineSegment(sketch, "E213.left", {"start": v(5.59, -12.26) * mm, "end": v(5.59, -8.26) * mm});
            skLineSegment(sketch, "E213.right", {"start": v(-5.59, -12.26) * mm, "end": v(-5.59, -8.26) * mm});
            skPoint(sketch, "E213.middle", {"position": v(0, -10.26) * mm});
            skPoint(sketch, "E214.MirrorP", {"position": v(0, 10.28) * mm});
            skLineSegment(sketch, "E215.MirrorCS", {"start": v(5.59, 12.28) * mm, "end": v(-5.59, 12.28) * mm});
            skLineSegment(sketch, "E216.MirrorCS", {"start": v(-5.59, 12.28) * mm, "end": v(-5.59, 8.28) * mm});
            skLineSegment(sketch, "E217.MirrorCS", {"start": v(5.59, 8.28) * mm, "end": v(-5.59, 8.28) * mm});
            skLineSegment(sketch, "E218.MirrorCS", {"start": v(5.59, 12.28) * mm, "end": v(5.59, 8.28) * mm});
            skSolve(sketch);
        }
        {
            var Q0;
            Q0 = qSketchRegion(id + "F23", true);
            extrude(context, id + "F24", {"entities" : qUnion([Q0]), "operationType" : NewBodyOperationType.ADD, "depth" : 5.7 * mm, "offsetDistance" : 25 * mm});
        }
        {
            var Q0;
            Q0=makeQuery(id+"F2.opExtrude","CAP_FACE",FACE,{"disambiguationData":[OSD([sQuery(id+"F0.wireOp",EDGE,"E0.bottom"),sQuery(id+"F0.wireOp",EDGE,"E0.top"),sQuery(id+"F0.wireOp",EDGE,"E0.left"),sQuery(id+"F0.wireOp",EDGE,"E0.right"),sQuery(id+"F0.wireOp",EDGE,"E1.bottom"),sQuery(id+"F0.wireOp",EDGE,"E1.top"),sQuery(id+"F0.wireOp",EDGE,"E1.left"),sQuery(id+"F0.wireOp",EDGE,"E1.right")])],"isStart":false});
            var sketch = newSketch(context, id + "F25", { "sketchPlane" : qUnion([Q0])});
            skLineSegment(sketch, "E219.bottom", {"start": v(-8.26, 8.26) * mm, "end": v(-10.35, 8.26) * mm});
            skLineSegment(sketch, "E219.top", {"start": v(-8.26, -8.3) * mm, "end": v(-10.35, -8.3) * mm});
            skLineSegment(sketch, "E219.left", {"start": v(-8.26, 8.26) * mm, "end": v(-8.26, -8.3) * mm});
            skLineSegment(sketch, "E219.right", {"start": v(-10.35, 8.26) * mm, "end": v(-10.35, -8.3) * mm});
            skLineSegment(sketch, "E220.MirrorCS", {"start": v(8.26, 8.26) * mm, "end": v(10.35, 8.26) * mm});
            skLineSegment(sketch, "E221.MirrorCS", {"start": v(10.35, 8.26) * mm, "end": v(10.35, -8.3) * mm});
            skLineSegment(sketch, "E222.MirrorCS", {"start": v(8.26, 8.26) * mm, "end": v(8.26, -8.3) * mm});
            skLineSegment(sketch, "E223.MirrorCS", {"start": v(8.26, -8.3) * mm, "end": v(10.35, -8.3) * mm});
            skLineSegment(sketch, "E224.bottom", {"start": v(-10.35, -8.3) * mm, "end": v(10.37, -8.3) * mm});
            skLineSegment(sketch, "E224.top", {"start": v(-10.35, -10.01) * mm, "end": v(10.37, -10.01) * mm});
            skLineSegment(sketch, "E224.left", {"start": v(-10.35, -8.3) * mm, "end": v(-10.35, -10.01) * mm});
            skLineSegment(sketch, "E224.right", {"start": v(10.37, -8.3) * mm, "end": v(10.37, -10.01) * mm});
            skLineSegment(sketch, "E225.MirrorCS", {"start": v(-10.35, 10.01) * mm, "end": v(10.37, 10.01) * mm});
            skLineSegment(sketch, "E226.MirrorCS", {"start": v(10.37, 8.3) * mm, "end": v(10.37, 10.01) * mm});
            skLineSegment(sketch, "E227.MirrorCS", {"start": v(-10.35, 8.3) * mm, "end": v(10.37, 8.3) * mm});
            skLineSegment(sketch, "E228.MirrorCS", {"start": v(-10.35, 8.3) * mm, "end": v(-10.35, 10.01) * mm});
            skSolve(sketch);
        }
        {
            var Q0;
            Q0 = qSketchRegion(id + "F25", true);
            extrude(context, id + "F26", {"entities" : qUnion([Q0]), "oppositeDirection" : true, "depth" : 1.65 * mm, "offsetDistance" : 25 * mm});
        }
        {
            var Q0;
            Q0=makeQuery(id+"F26.opExtrude","CAP_FACE",FACE,{"disambiguationData":[OSD([sQuery(id+"F25.wireOp",EDGE,"E219.bottom"),sQuery(id+"F25.wireOp",EDGE,"E219.left"),sQuery(id+"F25.wireOp",EDGE,"E219.right"),sQuery(id+"F25.wireOp",EDGE,"E220.MirrorCS"),sQuery(id+"F25.wireOp",EDGE,"E221.MirrorCS"),sQuery(id+"F25.wireOp",EDGE,"E222.MirrorCS"),sQuery(id+"F25.wireOp",EDGE,"E224.bottom"),sQuery(id+"F25.wireOp",EDGE,"E224.top"),sQuery(id+"F25.wireOp",EDGE,"E224.left"),sQuery(id+"F25.wireOp",EDGE,"E224.right")])],"isStart":true});
            var sketch = newSketch(context, id + "F27", { "sketchPlane" : qUnion([Q0])});
            skLineSegment(sketch, "E229", {"start": v(-8.26, 6.67) * mm, "end": v(-8.26, -6.67) * mm});
            skLineSegment(sketch, "E230", {"start": v(8.26, 6.67) * mm, "end": v(8.26, -6.67) * mm});
            skCircle(sketch, "E231", {"center": v(-8.26, 3.81) * mm, "radius": 0.25 * mm});
            skCircle(sketch, "E232", {"center": v(-8.26, 1.27) * mm, "radius": 0.25 * mm});
            skCircle(sketch, "E233", {"center": v(-8.26, -3.8) * mm, "radius": 0.25 * mm});
            skCircle(sketch, "E234", {"center": v(-8.26, -1.27) * mm, "radius": 0.25 * mm});
            skLineSegment(sketch, "E235", {"start": v(0, 0) * mm, "end": v(0, -7.63) * mm});
            skCircle(sketch, "E236.MirrorC", {"center": v(8.26, 1.27) * mm, "radius": 0.25 * mm});
            skCircle(sketch, "E237.MirrorC", {"center": v(8.26, -1.27) * mm, "radius": 0.25 * mm});
            skCircle(sketch, "E238.MirrorC", {"center": v(8.26, -3.8) * mm, "radius": 0.25 * mm});
            skCircle(sketch, "E239.MirrorC", {"center": v(8.26, 3.81) * mm, "radius": 0.25 * mm});
            skSolve(sketch);
        }
        {
            var Q0;
            Q0 = qSketchRegion(id + "F27", true);
            extrude(context, id + "F28", {"entities" : qUnion([Q0]), "operationType" : NewBodyOperationType.REMOVE, "oppositeDirection" : true, "depth" : 1.65 * mm, "offsetDistance" : 25 * mm});
        }
    });
